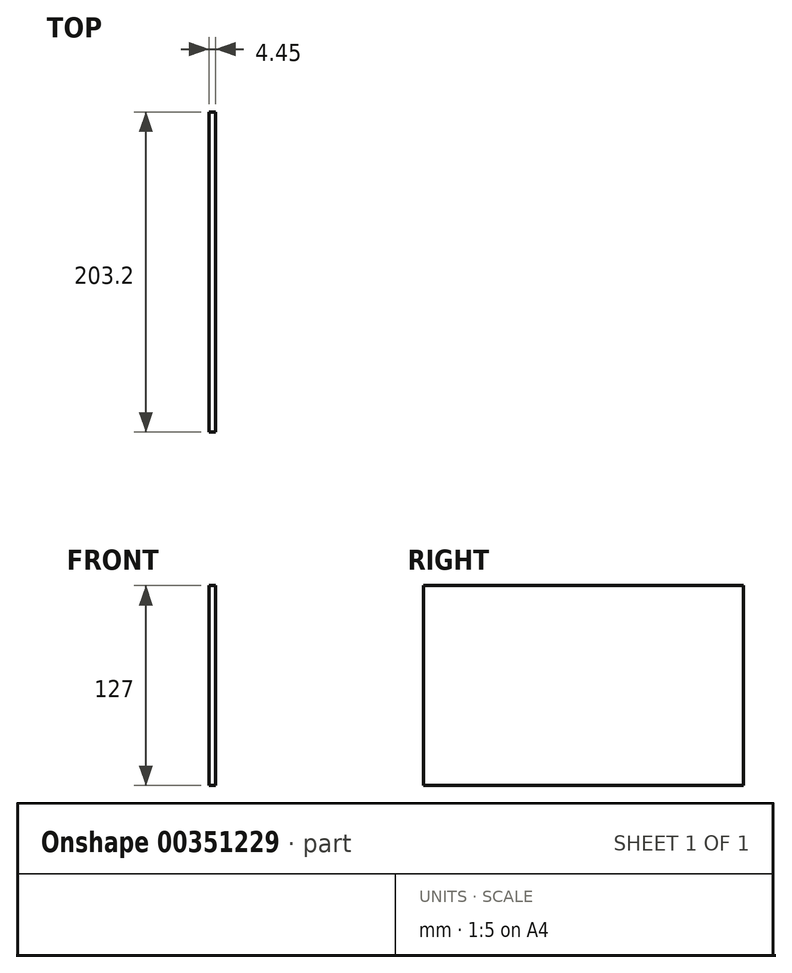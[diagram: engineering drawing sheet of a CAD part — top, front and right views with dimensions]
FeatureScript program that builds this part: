
annotation { "Feature Type Name" : "Feature", "Feature Type Description" : "" }
export const myFeature = defineFeature(function(context is Context, id is Id, definition is map)
    precondition{}
    {
        {
            var Q0;
            Q0=qCreatedBy(makeId("Right.planeOp"),FACE);
            var sketch = newSketch(context, id + "F0", { "sketchPlane" : qUnion([Q0])});
            skLineSegment(sketch, "E0", {"start": v(-97.74, 76.24) * mm, "end": v(105.46, 76.24) * mm});
            skLineSegment(sketch, "E1", {"start": v(105.46, 76.24) * mm, "end": v(105.46, -50.76) * mm});
            skLineSegment(sketch, "E2", {"start": v(105.46, -50.76) * mm, "end": v(-97.74, -50.76) * mm});
            skLineSegment(sketch, "E3", {"start": v(-97.74, -50.76) * mm, "end": v(-97.74, 76.24) * mm});
            skSolve(sketch);
        }
        {
            var Q0;
            Q0 = qSketchRegion(id + "F0", true);
            extrude(context, id + "F1", {"entities" : qUnion([Q0]), "depth" : 4.44 * mm});
        }
    });
